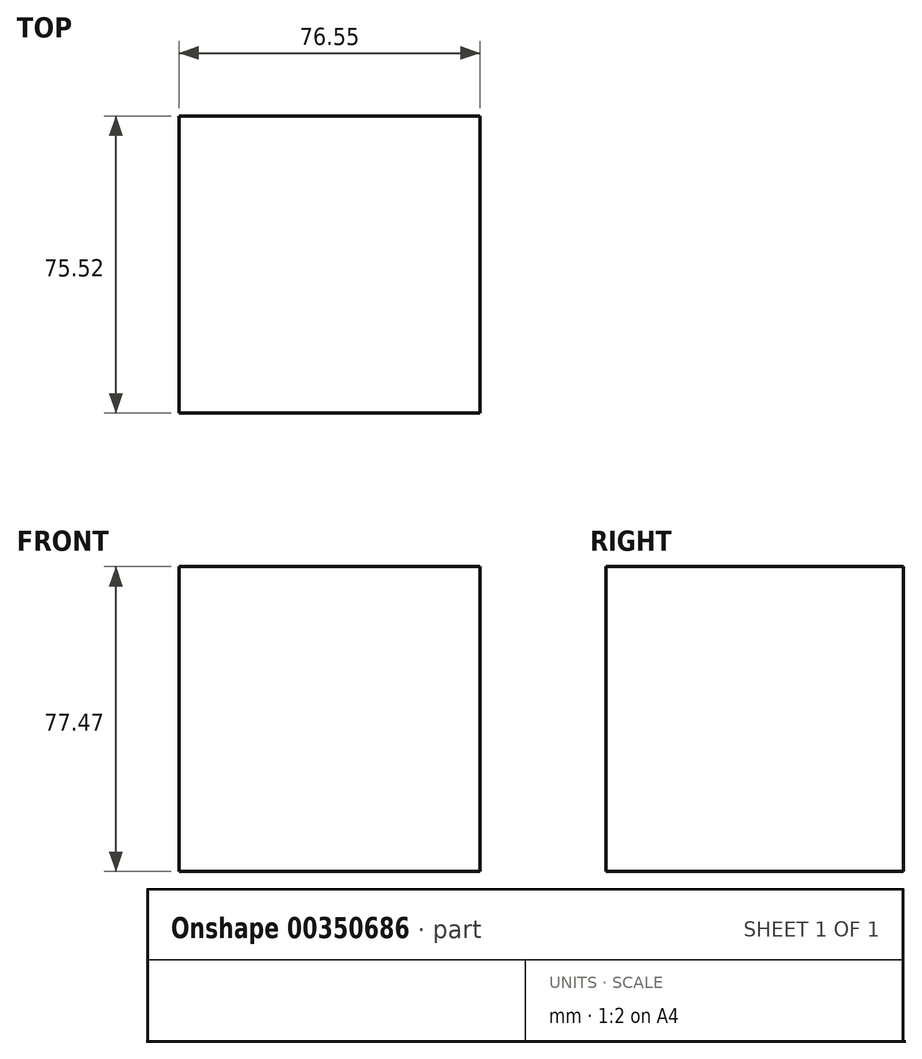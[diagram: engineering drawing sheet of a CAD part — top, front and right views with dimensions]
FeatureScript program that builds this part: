
annotation { "Feature Type Name" : "Feature", "Feature Type Description" : "" }
export const myFeature = defineFeature(function(context is Context, id is Id, definition is map)
    precondition{}
    {
        {
            var Q0;
            Q0=qCreatedBy(makeId("Top.planeOp"),FACE);
            var sketch = newSketch(context, id + "F0", { "sketchPlane" : qUnion([Q0])});
            skLineSegment(sketch, "E0.bottom", {"start": v(0, 0) * mm, "end": v(-76.55, 0) * mm});
            skLineSegment(sketch, "E0.top", {"start": v(0, -75.52) * mm, "end": v(-76.55, -75.52) * mm});
            skLineSegment(sketch, "E0.left", {"start": v(0, 0) * mm, "end": v(0, -75.52) * mm});
            skLineSegment(sketch, "E0.right", {"start": v(-76.55, 0) * mm, "end": v(-76.55, -75.52) * mm});
            skSolve(sketch);
        }
        {
            var Q0;
            Q0 = qSketchRegion(id + "F0", true);
            var Q1;
            Q1=makeQuery(id+"F0.imprint","IMPRINT",FACE,{"disambiguationData":[TD([[makeQuery(id+"F0.imprint","IMPRINT",EDGE,{"derivedFrom":sQuery(id+"F0.wireOp",EDGE,"E0.bottom")}),1.0]])]});
            extrude(context, id + "F1", {"entities" : qUnion([Q0, Q1]), "depth" : 77.47 * mm});
        }
    });
